FCSTD DOCUMENT  (FreeCAD 1.0R39109 (Git))
Label: Master Document
License: All rights reserved
LicenseURL: http://en.wikipedia.org/wiki/All_rights_reserved
objects: Spreadsheet::Sheet×1

FEATURE [Spreadsheet::Sheet] Spreadsheet  label="Monitor Chassis Parameters"
  cells = A1='Parameter Name; B1='Value; C1='Notes; A2='GSWallWidth; B2(GSWallWidth)=123; A3='GSBaseFloorBeamWidth; B3(GSBaseFloorBeamWidth)==B31 * 3; C3='Is relelative to the size of the screw hole size; A4='GSBaseBodyThickness; B4(GSBaseBodyThickness)=3; A5='GSCamWallThickness; B5(GSCamWallThickness)=4; A6='GSThinWallThickness; B6(GSThinWallThickness)=3; A7='GSCamWallClickIndent; B7(GSCamWallClickIndent)=1; A8='GSCamWallClickLength; B8(GSCamWallClickLength)=6; A9='GSCamWallFullClickStructureHeight; B9(GSCamWallFullClickStructureHeight)=20; A12='GSCamBoardHeight; B12(GSCamBoardHeight)=38; A13='GSCamBoardWidth; B13(GSCamBoardWidth)=38; A14='GSCamBoardMountingHoleDiameter; B14(GSCamBoardMountingHoleDiameter)==B40; A15='GSCamPlateThickness; B15(GSCamPlateThickness)=4; A16='GSCamMountingHoleOffset; B16(GSCamMountingHoleOffset)=4; A17='GSCamMountingHoleThickness; B17(GSCamMountingHoleThickness)=2; A18='GSCamMountingHoleHeight; B18(GSCamMountingHoleHeight)=7; A19='GSCamAxisHoleDiameter; B19(GSCamAxisHoleDiameter)==B41; C19='M4 uses a 4.5 mm hole; A20='GSCamAxisWidth; B20(GSCamAxisWidth)=22; A21='GSCamMountingIndentInnerDiameter; B21(GSCamMountingIndentInnerDiameter)=5; C21='TBD - Not a good name?; A22='GSCamMountingHoleDiameter; B22(GSCamMountingHoleDiameter)=2.5; A23='GSCamGimbalDepth; B23(GSCamGimbalDepth)=20; A24='GSCam1ZAxisSetback; B24(GSCam1ZAxisSetback)=15; C24='The camera will be mounted back, away from the lens to help the tilt ability; A25='GSCam2ZAxisSetback; B25(GSCam2ZAxisSetback)=15; C25='The camera will be mounted back, away from the lens to help the tilt ability; A26='GSCamGimbalLighteningSlotOffsetFromCenter; B26(GSCamGimbalLighteningSlotOffsetFromCenter)=12; A27='GSCamGimbalInnerLength; B27(GSCamGimbalInnerLength)=58; A28='GSCam1GimbalHoleHeight; B28(GSCam1GimbalHoleHeight)=50; A29='GSCam2GimbalHoleHeight; B29(GSCam2GimbalHoleHeight)=35; A30='GSCamM4NutHexagonDiameter; B30(GSCamM4NutHexagonDiameter)=8.4; A31='GSCamM4ScrewHoleDiameter; B31(GSCamM4ScrewHoleDiameter)=3.3; A32='GSCamM4NutDepth; B32(GSCamM4SNutDepth)=4; A33='GSCamM3NutDepth; B33(GSCamM3NutDepth)=3.5; A34='GSCamM5NutHexagonDiameter; B34(GSCamM5NutHexagonDiameter)=9.5; A35='GSCamM3NutHexagonDiameter; B35(GSCamM3NutHexagonDiameter)=6.6; A36='GSCamM5ScrewHoleDiameter; B36(GSCamM5ScrewHoleDiameter)=5.5; A37='GSCamM5NutDepth; B37(GSCamM5NutDepth)=4; A38='GSLEDPowerRiserHeight; B38(GSLEDPowerRiserHeight)=7; A39='GSM3BoltHoleDiameter; B39(GSM3BoltHoleDiameter)=3.4; A40='GSM25BoltHoleDiameter; B40(GSM25BoltHoleDiameter)=2.9; A41='GSM4BoltHoleDiameter; B41(GSM4BoltHoleDiameter)=4.5; A42='GSM4BoltHeadIndentDiameter; B42(GSM4BoltHeadIndentDiameter)=7.5; A44='GSM3TappingScrewHoleDiameter; B44(GSM3TappingScrewHoleDiameter)=2.4; A46='GSMonitorFloorPowerBayLength; B46(GSMonitorFloorPowerBayLength)=155
